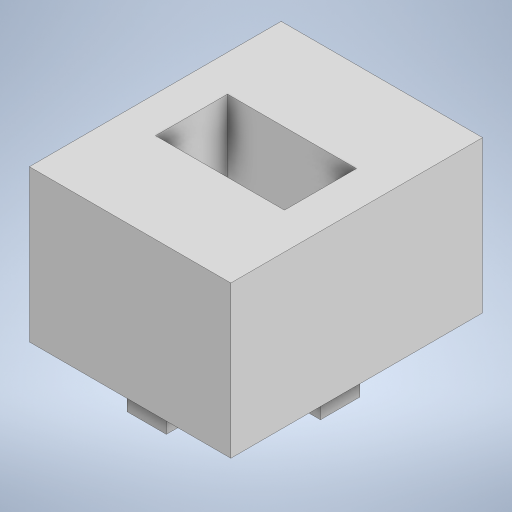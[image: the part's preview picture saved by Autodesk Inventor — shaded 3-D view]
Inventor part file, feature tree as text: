
AUTODESK INVENTOR PART (.ipt)
format: ipt  version: 2023 (Build 270158000, 158)  size: 249,856 bytes
history: native  units: in
note: dims shown in document units (in); Inventor stores cm internally (conversion verified against a paired STEP export)
features: extrude x6, sketch x6, mirror x4
ambient origin geometry x8: Origin, YZ Plane, XZ Plane, XY Plane, X Axis, Y Axis, Z Axis, Center Point
bodies: Solid1 (feature_tree)
feature tree (16):
  extrude  "Extrusion1"  Depth=0.64in
  extrude  "Extrusion2"  Depth=0.2287in
  extrude  "Extrusion3"  TaperAngle=0.0deg  [1 undecoded]
  mirror  "Mirror1"
  extrude  "Extrusion4"  Depth=0.387in
  mirror  "Mirror2"
  extrude  "Extrusion5"  Depth=0.1027in TaperAngle=0.0deg
  mirror  "Mirror3"
  extrude  "Extrusion6"  Depth=0.0625in
  mirror  "Mirror4"
  sketch  "Sketch1"  dims[d0=0.8in d1=0.64in]
  sketch  "Sketch3"  dims[d2=0.4823in d3=0.0in d4=0.2287in]
  sketch  "Sketch4"  dims[d5=0.4097in d6=0.0in d7=0.0in]
  sketch  "Sketch5"  dims[d8=0.112in d9=0.387in]
  sketch  "Sketch6"  dims[d10=0.275in d11=0.1027in d12=0.0in]
  sketch  "Sketch7"  dims[d13=0.0098in d14=0.0625in d15=0.125in d16=0.0893in d17=0.0in d18=0.0625in d19=0.125in d20=0.0893in d21=0.0in d22=0.01in d23=0.0244in d24=0.0in]
note: 1 required parameter value undecoded (feature->parameter linkage not recoverable at this tier; creation-order binding heuristic only, values carry confidence <= 0.55)
